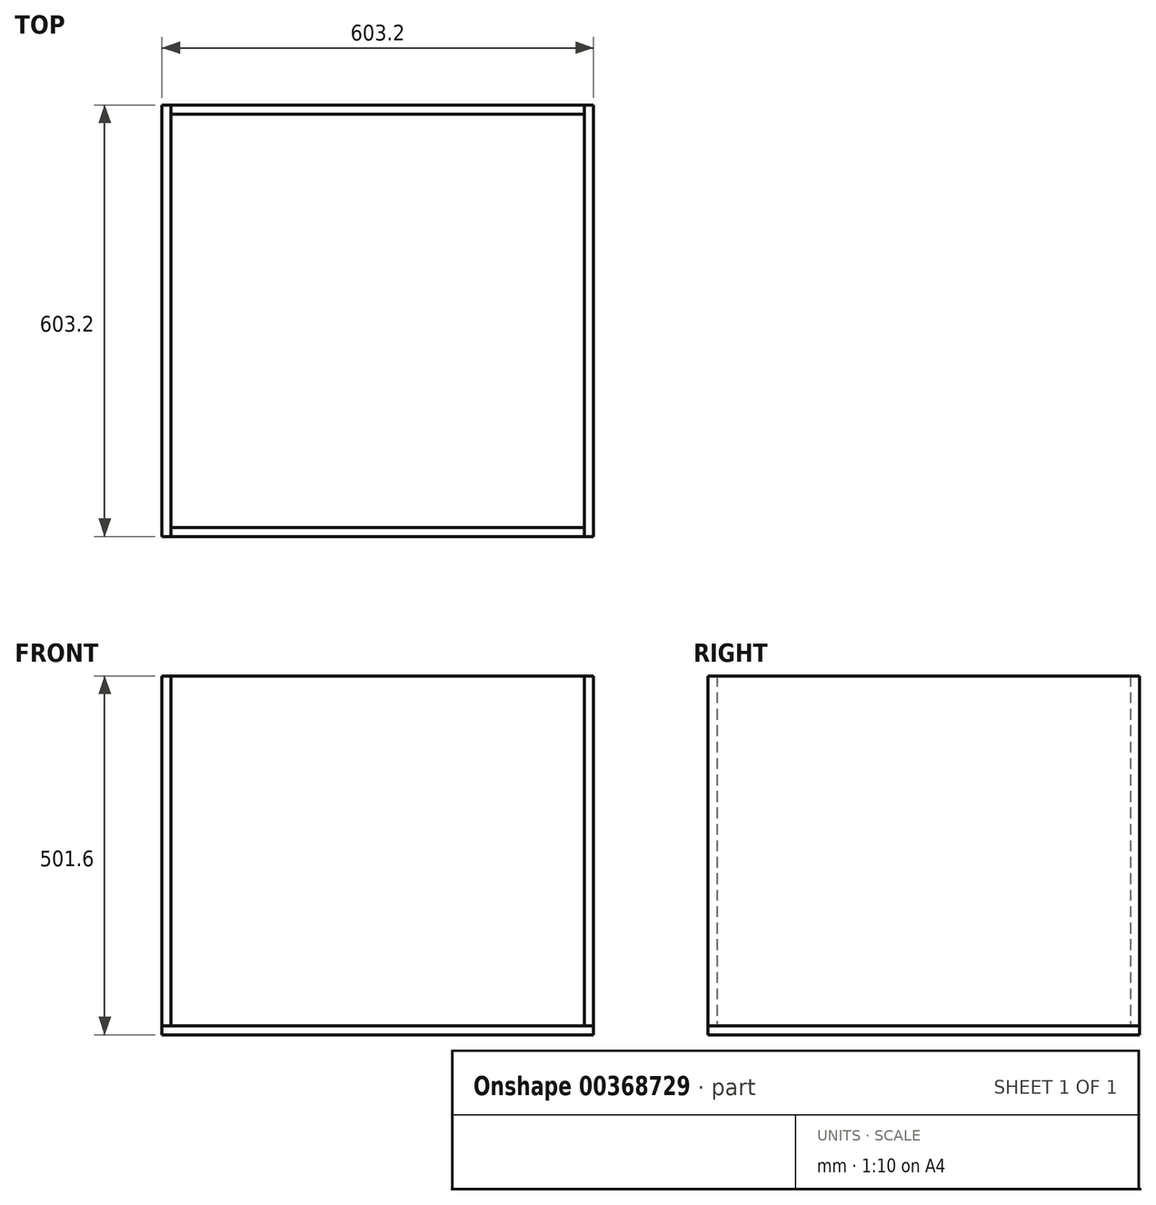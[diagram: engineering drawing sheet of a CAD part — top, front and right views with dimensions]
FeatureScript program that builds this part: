
annotation { "Feature Type Name" : "Feature", "Feature Type Description" : "" }
export const myFeature = defineFeature(function(context is Context, id is Id, definition is map)
    precondition{}
    {
        {
            var Q0;
            Q0=qCreatedBy(makeId("Top.planeOp"),FACE);
            var sketch = newSketch(context, id + "F0", { "sketchPlane" : qUnion([Q0])});
            skPoint(sketch, "E0.middle", {"position": v(0, 0) * mm});
            skLineSegment(sketch, "E1.bottom", {"start": v(288.9, 288.9) * mm, "end": v(-288.9, 288.9) * mm});
            skLineSegment(sketch, "E1.top", {"start": v(288.9, -288.9) * mm, "end": v(-288.9, -288.9) * mm});
            skLineSegment(sketch, "E1.left", {"start": v(288.9, 288.9) * mm, "end": v(288.9, -288.9) * mm});
            skLineSegment(sketch, "E1.right", {"start": v(-288.9, 288.9) * mm, "end": v(-288.9, -288.9) * mm});
            skLineSegment(sketch, "E2.bottom", {"start": v(301.6, 301.6) * mm, "end": v(-301.6, 301.6) * mm});
            skLineSegment(sketch, "E2.top", {"start": v(301.6, -301.6) * mm, "end": v(-301.6, -301.6) * mm});
            skLineSegment(sketch, "E2.left", {"start": v(301.6, 301.6) * mm, "end": v(301.6, -301.6) * mm});
            skLineSegment(sketch, "E2.right", {"start": v(-301.6, 301.6) * mm, "end": v(-301.6, -301.6) * mm});
            skLineSegment(sketch, "E3", {"start": v(-288.9, 288.9) * mm, "end": v(-288.9, 301.6) * mm});
            skLineSegment(sketch, "E4", {"start": v(288.9, 288.9) * mm, "end": v(288.9, 301.6) * mm});
            skLineSegment(sketch, "E5", {"start": v(288.9, -288.9) * mm, "end": v(288.9, -301.6) * mm});
            skLineSegment(sketch, "E6", {"start": v(-288.9, -288.9) * mm, "end": v(-288.9, -301.6) * mm});
            skSolve(sketch);
        }
        {
            var Q0;
            Q0=makeQuery(id+"F0.imprint","IMPRINT",FACE,{"disambiguationData":[TD([[makeQuery(id+"F0.imprint","IMPRINT",EDGE,{"derivedFrom":sQuery(id+"F0.wireOp",EDGE,"E1.bottom")}),1.0]])]});
            var Q1;
            Q1=makeQuery(id+"F0.imprint","IMPRINT",FACE,{"disambiguationData":[TD([[makeQuery(id+"F0.imprint","IMPRINT",EDGE,{"derivedFrom":sQuery(id+"F0.wireOp",EDGE,"E1.right")}),-1.0]])]});
            var Q2;
            Q2=makeQuery(id+"F0.imprint","IMPRINT",FACE,{"disambiguationData":[TD([[makeQuery(id+"F0.imprint","IMPRINT",EDGE,{"derivedFrom":sQuery(id+"F0.wireOp",EDGE,"E1.bottom")}),-1.0]])]});
            var Q3;
            Q3=makeQuery(id+"F0.imprint","IMPRINT",FACE,{"disambiguationData":[TD([[makeQuery(id+"F0.imprint","IMPRINT",EDGE,{"derivedFrom":sQuery(id+"F0.wireOp",EDGE,"E1.left")}),1.0]])]});
            var Q4;
            Q4=makeQuery(id+"F0.imprint","IMPRINT",FACE,{"disambiguationData":[TD([[makeQuery(id+"F0.imprint","IMPRINT",EDGE,{"derivedFrom":sQuery(id+"F0.wireOp",EDGE,"E1.top")}),1.0]])]});
            extrude(context, id + "F1", {"entities" : qUnion([Q0, Q1, Q2, Q3, Q4]), "oppositeDirection" : true, "depth" : 12.7 * mm});
        }
        {
            var Q0;
            Q0=makeQuery(id+"F0.imprint","IMPRINT",FACE,{"disambiguationData":[TD([[makeQuery(id+"F0.imprint","IMPRINT",EDGE,{"derivedFrom":sQuery(id+"F0.wireOp",EDGE,"E1.bottom")}),-1.0]])]});
            extrude(context, id + "F2", {"entities" : qUnion([Q0]), "depth" : 400 * mm + 76.2 * mm + 12.7 * mm});
        }
        {
            var Q0;
            Q0=makeQuery(id+"F0.imprint","IMPRINT",FACE,{"disambiguationData":[TD([[makeQuery(id+"F0.imprint","IMPRINT",EDGE,{"derivedFrom":sQuery(id+"F0.wireOp",EDGE,"E1.right")}),-1.0]])]});
            extrude(context, id + "F3", {"entities" : qUnion([Q0]), "depth" : 400 * mm + 76.2 * mm + 12.7 * mm});
        }
        {
            var Q0;
            Q0=makeQuery(id+"F0.imprint","IMPRINT",FACE,{"disambiguationData":[TD([[makeQuery(id+"F0.imprint","IMPRINT",EDGE,{"derivedFrom":sQuery(id+"F0.wireOp",EDGE,"E1.left")}),1.0]])]});
            extrude(context, id + "F4", {"entities" : qUnion([Q0]), "depth" : 400 * mm + 76.2 * mm + 12.7 * mm});
        }
        {
            var Q0;
            Q0=makeQuery(id+"F0.imprint","IMPRINT",FACE,{"disambiguationData":[TD([[makeQuery(id+"F0.imprint","IMPRINT",EDGE,{"derivedFrom":sQuery(id+"F0.wireOp",EDGE,"E1.top")}),1.0]])]});
            extrude(context, id + "F5", {"entities" : qUnion([Q0]), "depth" : 400 * mm + 76.2 * mm + 12.7 * mm});
        }
    });
